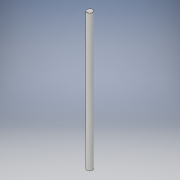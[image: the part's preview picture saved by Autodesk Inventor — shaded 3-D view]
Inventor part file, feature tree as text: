
AUTODESK INVENTOR PART (.ipt)
format: ipt  version: 2017 (Build 210142000, 142)  size: 109,056 bytes
history: native  units: in
note: dims shown in document units (in); Inventor stores cm internally (conversion verified against a paired STEP export)
features: direct_edit x1, chamfer x1, move_body x1
ambient origin geometry x8: Origin, YZ Plane, XZ Plane, XY Plane, X Axis, Y Axis, Z Axis, Center Point
bodies: Solid1 (feature_tree)
feature tree (3):
  direct_edit  "Direct Edit1"
  chamfer  "Chamfer1"  [1 undecoded]
  move_body  "Move1"
note: 1 required parameter value undecoded (feature->parameter linkage not recoverable at this tier; creation-order binding heuristic only, values carry confidence <= 0.55)
